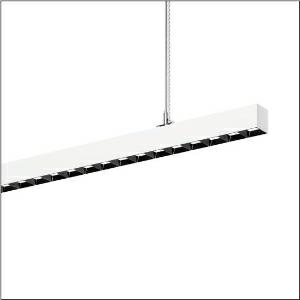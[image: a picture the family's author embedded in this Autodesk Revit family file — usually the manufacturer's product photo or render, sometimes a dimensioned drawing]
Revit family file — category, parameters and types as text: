
# Revit family: silica_r__21_51mx32dc3dwb_4ada
name_source: partatom
category: Lighting Fixtures
units: mm (PartAtom-declared; Revit-internal decimal feet)

## family parameters
Cut with Voids When Loaded = No
Host = Face
Light Source = No
Part Type = Normal
Room Calculation Point = No
Round Connector Dimension = Use Diameter
Shared = No

## types (1)
- --- (1 x LED, 18220 lm, 113 W, 3000K)
    Apparent Load = 113 VA
    CIE Flux Codes = 86 99 100 59 100
    Color Rendering = 80
    Color Temperature = 3000K
    Default Elevation = 1800 mm
    Description = Silica® 21, office luminaire, primary light control with darklight reflector, of PMMA, black, CAT 2 (L<= 3000cd/m²), light emission: direct/indirect distribution, primary light characteristic: symmetric, installation type: suspended mounting, LED, rated luminous flux: 18.220lm, luminous efficacy: 161lm/W, light colour: 830, colour temperature: 3000K, with terminal, 3+2-pole, max. 2.5mm², mains connection: 220..240V, AC, 50/60Hz, rated input power: 113W, luminaire housing, of aluminium, traffic white (RAL 9016), length: 3.004mm, width: 53mm, height: 53mm, protection rating (complete): IP20, insulation class (complete): insulation class I (protective earthing), certification: CE, permissible operating ambient temperature: 0..+35°C, standard: EN 50419, packaging unit: 1 piece
    Height = 53 mm
    Lamp = 1 x LED
    Lamp Light Flux = 18220 lm
    Lamp Power = 113 W
    Lamp count = 1
    Length = 3004 mm
    Luminous efficacy = 161 lm/W
    Manufacturer = Siteco
    ModVariant = No
    Model = 51MX32DC3DWB
    Mounting Place = Ceiling
    Mounting Type = Pendant
    Number of Poles = 1
    OnlyDefault = Yes
    Power Factor = 1
    Product Name = Silica® 21
    Product group = office luminaire | ceiling pendant
    ProductGroupID = 905
    Protection Class = Protection class I
    Protection Degree = IP 20
    RLX_Detail_Level = 1
    RlxData = <blob elided: 64589 chars, md5=9b364ccc>
    Socket = socket
    Standby Power = 0 W
    System Light Flux = 18220 lm
    System Power = 113 W
    Type Comments = factory setting: luminous flux: 100 % | dim-lin: 254 | 391 mA
    Type Image = l_1251637.jpg
    URL = http://relux.com
    VarID = @adj_031379
    Voltage = 0 V
    Weight = 0.00 kg
    Width = 53 mm

## geometry (parser evidence)
native form markers: Blend x4, Sweep x11
no freeform markers — native parametric forms only
